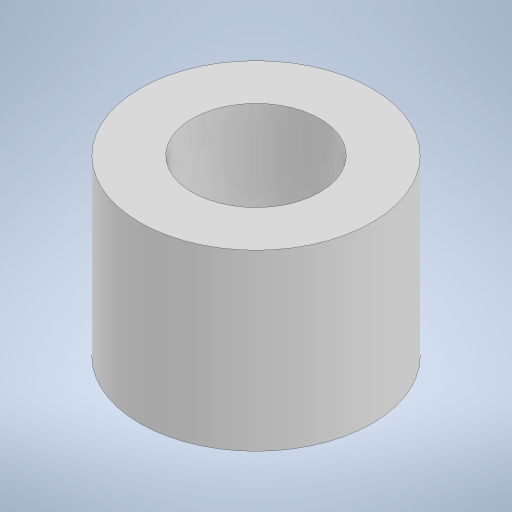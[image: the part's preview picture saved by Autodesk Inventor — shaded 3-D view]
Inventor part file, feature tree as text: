
AUTODESK INVENTOR PART (.ipt)
format: ipt  version: 2023 (Build 270158000, 158)  size: 193,536 bytes
history: native  units: mm
features: extrude x1, sketch x1
ambient origin geometry x8: Origin, YZ Plane, XZ Plane, XY Plane, X Axis, Y Axis, Z Axis, Center Point
bodies: Solid1 (feature_tree)
feature tree (2):
  extrude  "Extrusion1"  Depth=6.0mm
  sketch  "Sketch1"  dims[d0=4.4mm d1=8.0mm d2=6.0mm d3=0.0mm]
